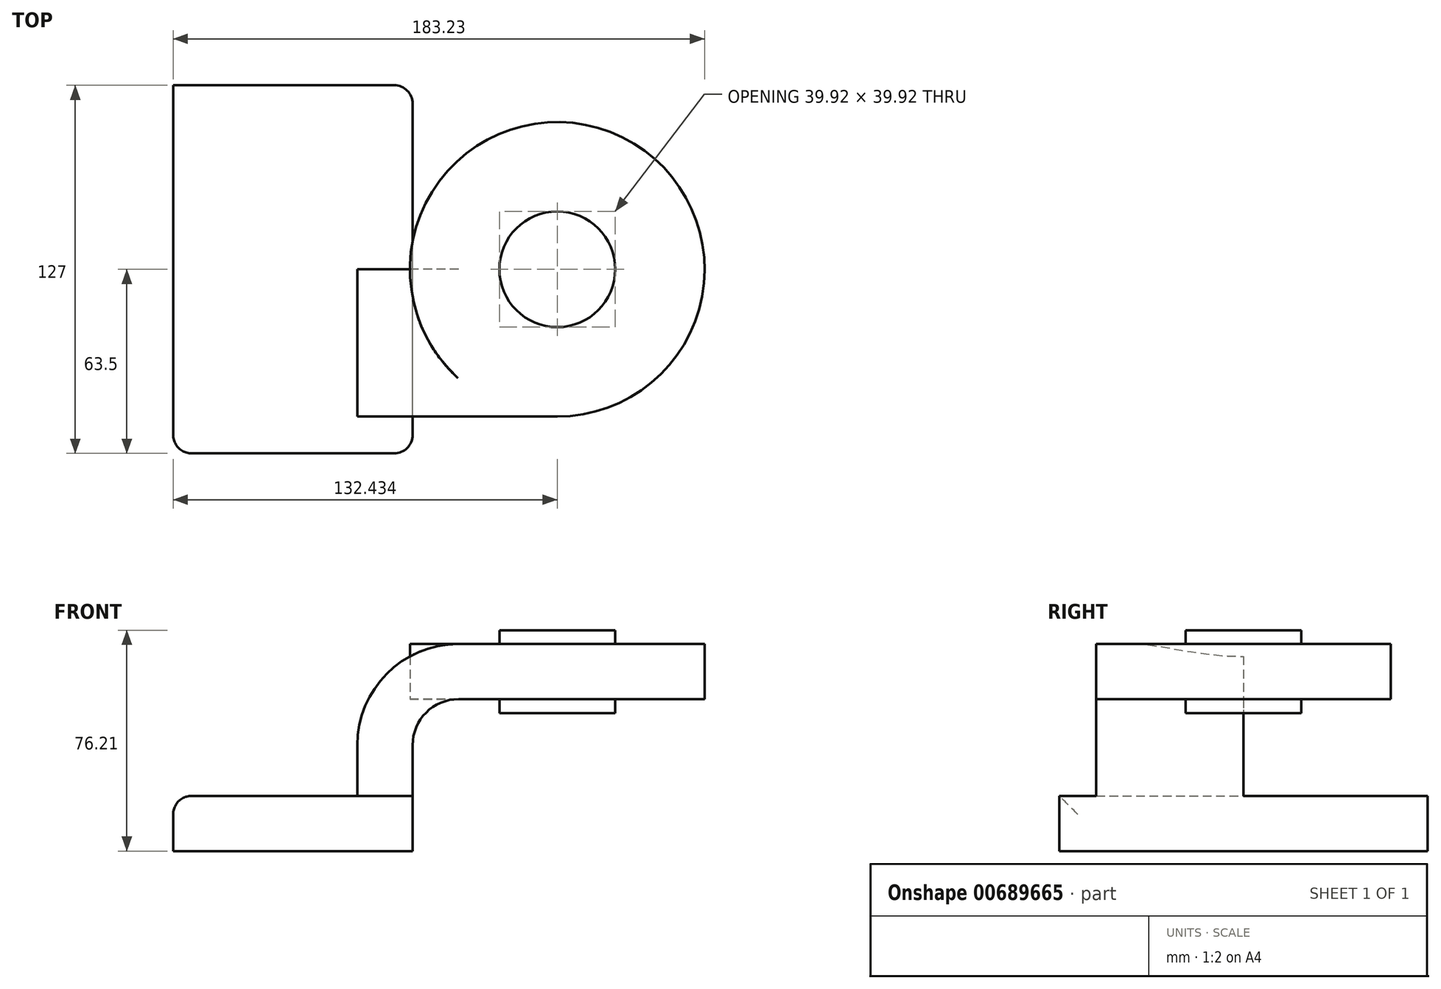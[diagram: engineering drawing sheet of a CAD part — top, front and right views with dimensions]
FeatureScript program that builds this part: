
annotation { "Feature Type Name" : "Feature", "Feature Type Description" : "" }
export const myFeature = defineFeature(function(context is Context, id is Id, definition is map)
    precondition{}
    {
        {
            var Q0;
            Q0=qCreatedBy(makeId("Front.planeOp"),FACE);
            var sketch = newSketch(context, id + "F0", { "sketchPlane" : qUnion([Q0])});
            skLineSegment(sketch, "E0.bottom", {"start": v(41.28, -9.52) * mm, "end": v(-41.28, -9.53) * mm});
            skLineSegment(sketch, "E0.top", {"start": v(41.28, 9.53) * mm, "end": v(-41.28, 9.53) * mm});
            skLineSegment(sketch, "E0.left", {"start": v(41.28, -9.52) * mm, "end": v(41.28, 9.53) * mm});
            skLineSegment(sketch, "E0.right", {"start": v(-41.28, -9.52) * mm, "end": v(-41.28, 9.53) * mm});
            skPoint(sketch, "E0.middle", {"position": v(0, 0) * mm});
            skLineSegment(sketch, "E1.bottom", {"start": v(111.12, 38.1) * mm, "end": v(60.32, 38.1) * mm});
            skLineSegment(sketch, "E1.top", {"start": v(111.12, 66.68) * mm, "end": v(60.33, 66.68) * mm});
            skLineSegment(sketch, "E1.left", {"start": v(111.12, 38.1) * mm, "end": v(111.12, 66.67) * mm});
            skLineSegment(sketch, "E1.right", {"start": v(60.33, 38.1) * mm, "end": v(60.33, 66.67) * mm});
            skPoint(sketch, "E1.middle", {"position": v(85.72, 52.39) * mm});
            skLineSegment(sketch, "E2", {"start": v(41.28, 9.53) * mm, "end": v(41.28, 27) * mm});
            skArc(sketch, "E3", {"start": v(41.27, 27) * mm, "mid": v(45.92, 38.23) * mm, "end": v(57.15, 42.88) * mm});
            skLineSegment(sketch, "E4", {"start": v(57.15, 42.88) * mm, "end": v(91.16, 42.88) * mm});
            skLineSegment(sketch, "E5.0", {"start": v(57.15, 61.93) * mm, "end": v(91.16, 61.93) * mm});
            skArc(sketch, "E5.1", {"start": v(22.23, 27) * mm, "mid": v(32.45, 51.7) * mm, "end": v(57.15, 61.93) * mm});
            skLineSegment(sketch, "E5.2", {"start": v(22.22, 9.53) * mm, "end": v(22.22, 27) * mm});
            skLineSegment(sketch, "E6", {"start": v(91.16, 38.1) * mm, "end": v(91.16, 66.68) * mm});
            skFitSpline(sketch, "E7", {"points": [v(-41.28, 9.52) * mm, v(57.15, 61.93) * mm], "startDerivative": vector(0.03, 106.67) * mm, "endDerivative": vector(126.07, 0.3) * mm});
            skSolve(sketch);
        }
        {
            var Q0;
            Q0=makeQuery(id+"F0.imprint","IMPRINT",FACE,{"disambiguationData":[TD([[makeQuery(id+"F0.imprint","IMPRINT",EDGE,{"derivedFrom":sQuery(id+"F0.wireOp",EDGE,"E0.bottom")}),-1.0]])]});
            extrude(context, id + "F1", {"entities" : qUnion([Q0]), "endBound" : BoundingType.SYMMETRIC, "depth" : 127 * mm, "offsetDistance" : 25.4 * mm});
        }
        {
            var Q0;
            {var subQ5=sQuery(id+"F0.wireOp",EDGE,"E2");Q0=makeQuery(id+"F0.imprint","IMPRINT",FACE,{"disambiguationData":[TD([[makeQuery(id+"F0.imprint","IMPRINT",EDGE,{"derivedFrom":subQ5}),1.0]])]});}
            var Q1;
            {var subQ0=sQuery(id+"F0.wireOp",EDGE,"E4");var subQ1=sQuery(id+"F0.wireOp",EDGE,"E1.right");var subQ2=makeQuery(id+"F0.imprint","INTERSECT",VERTEX,{"derivedFrom":[subQ1,subQ0]});Q1=makeQuery(id+"F0.imprint","IMPRINT",FACE,{"disambiguationData":[TD([[makeQuery(id+"F0.imprint","IMPRINT",EDGE,{"disambiguationData":[TD([[subQ2,-1.0]])],"derivedFrom":subQ1}),-1.0]])]});}
            extrude(context, id + "F2", {"entities" : qUnion([Q0, Q1]), "operationType" : NewBodyOperationType.ADD, "depth" : 50.8 * mm, "offsetDistance" : 25.4 * mm});
        }
        {
            var Q0;
            {var subQ4=sQuery(id+"F0.wireOp",EDGE,"E5.1");Q0=makeQuery(id+"F0.imprint","IMPRINT",FACE,{"disambiguationData":[TD([[makeQuery(id+"F0.imprint","IMPRINT",EDGE,{"derivedFrom":subQ4}),1.0]])]});}
            extrude(context, id + "F3", {"entities" : qUnion([Q0]), "operationType" : NewBodyOperationType.ADD, "depth" : 15.88 * mm, "offsetDistance" : 25.4 * mm});
        }
        {
            var Q0;
            {var subQ4=sQuery(id+"F0.wireOp",EDGE,"E1.left");Q0=makeQuery(id+"F0.imprint","IMPRINT",FACE,{"disambiguationData":[TD([[makeQuery(id+"F0.imprint","IMPRINT",EDGE,{"derivedFrom":subQ4}),1.0]])]});}
            var Q1;
            Q1=makeQuery(id+"F2.opExtrude","SWEPT_FACE",FACE,{"disambiguationData":[OSD([sQuery(id+"F0.wireOp",EDGE,"E6")])]});
            var Q2;
            Q2=sQuery(id+"F0.wireOp",EDGE,"E6");
            revolve(context, id + "F4", {"operationType" : NewBodyOperationType.ADD, "entities" : qUnion([Q0, Q1]), "axis" : qUnion([Q2]), "revolveType" : RevolveType.FULL});
        }
        {
            var Q0;
            Q0=makeQuery(id+"F1.opExtrude","CAP_EDGE",EDGE,{"disambiguationData":[OSD([sQuery(id+"F0.wireOp",EDGE,"E0.left")])],"isStart":false});
            var Q1;
            Q1=makeQuery(id+"F1.opExtrude","CAP_EDGE",EDGE,{"disambiguationData":[OSD([sQuery(id+"F0.wireOp",EDGE,"E0.right")])],"isStart":false});
            var Q2;
            {var subQ0=sQuery(id+"F0.wireOp",EDGE,"E7");var subQ3=sQuery(id+"F0.wireOp",EDGE,"E0.top");var subQ4=sQuery(id+"F0.wireOp",EDGE,"E0.right");Q2=makeQuery(id+"F3.boolean.opBoolean","SPLIT",EDGE,{"disambiguationData":[TD([makeQuery(id+"F1.opExtrude","CAP_FACE",FACE,{"disambiguationData":[OSD([sQuery(id+"F0.wireOp",EDGE,"E0.bottom"),subQ3,sQuery(id+"F0.wireOp",EDGE,"E0.left"),subQ4])],"isStart":true})])],"derivedFrom":makeQuery(id+"F1.opExtrude","SWEPT_EDGE",EDGE,{"disambiguationData":[OSD([subQ3,subQ4,subQ0])]})});}
            var Q3;
            Q3=makeQuery(id+"F1.opExtrude","CAP_EDGE",EDGE,{"disambiguationData":[OSD([sQuery(id+"F0.wireOp",EDGE,"E0.left")])],"isStart":true});
            fillet(context, id + "F5", {"entities" : qUnion([Q0, Q1, Q2, Q3]), "radius" : 6.35 * mm, "tangentPropagation" : true, "allowEdgeOverflow" : false});
        }
    });
